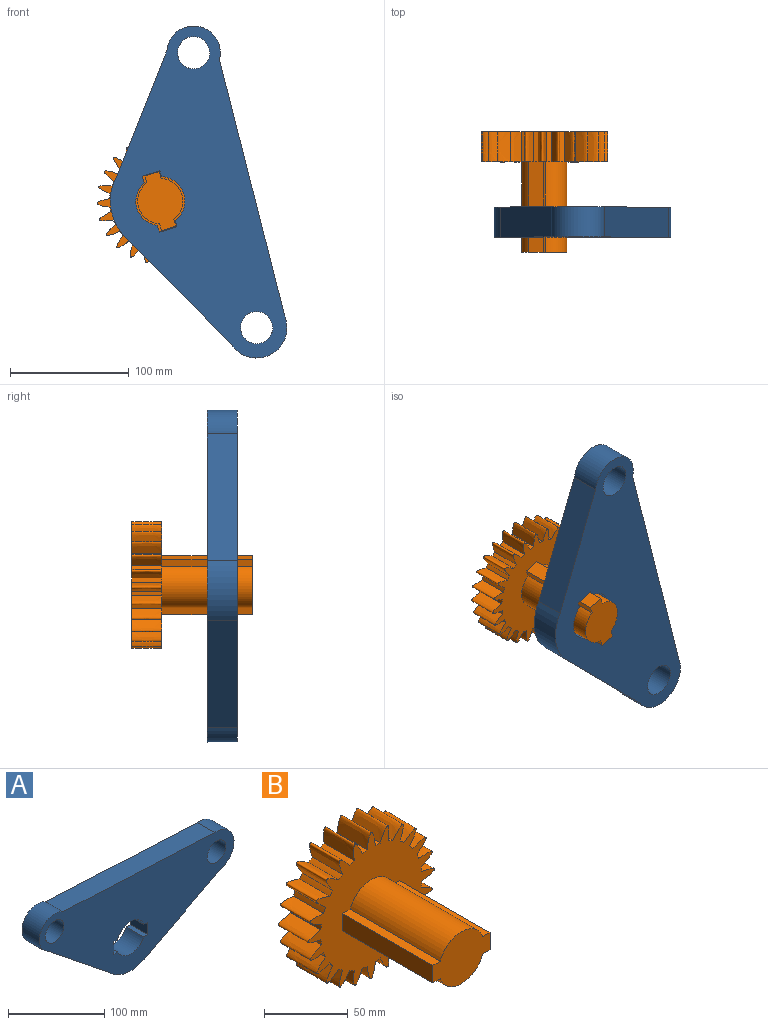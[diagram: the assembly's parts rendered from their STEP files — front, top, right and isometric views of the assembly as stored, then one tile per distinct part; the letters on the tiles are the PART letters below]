
ASSEMBLY  parts=2 mates=1
PART A: 18 faces, bbox 285.5x25.4x128.4 mm
  f0: plane 285.47x128.35mm, normal (0,-1,0), area 20341.7mm2, adj f2,f3,f4,f5,f6,f7,f8,f9
  f1: plane 285.47x128.35mm, normal (0,1,0), area 20341.7mm2, adj f2,f3,f4,f5,f6,f7,f8,f9
  f2: cylinder r=22.52mm len=43.27mm, axis (0,1,0), area 1890.6mm2, adj f0,f1,f3,f7
  f3: plane 89.47x71.82mm, normal (-0.63,0,-0.78), area 2914.1mm2, adj f0,f1,f2,f4
  f4: cylinder r=42.25mm len=50.29mm, axis (0,1,0), area 1390.7mm2, adj f0,f1,f3,f5
  f5: plane 112.86x58.95mm, normal (0.46,0,-0.89), area 3234.2mm2, adj f0,f1,f4,f6
  f6: cylinder r=25.63mm len=50.41mm, axis (0,1,0), area 1940.8mm2, adj f0,f1,f5,f7
  f7: plane 222.79x25.4mm, normal (0.05,0,1), area 5665.7mm2, adj f0,f1,f2,f6
  f8: cylinder r=20.68mm len=37.69mm, axis (0,1,0), area 1204.7mm2, adj f0,f1,f9,f15
  f9: plane 25.4x6.07mm, normal (0,0,1), area 154.1mm2, adj f0,f1,f8,f10
  f10: plane 25.4x15.55mm, normal (-1,0,0), area 395mm2, adj f0,f1,f9,f11
  f11: plane 25.4x5.48mm, normal (0,0,-1), area 139.1mm2, adj f0,f1,f10,f12
  f12: cylinder r=20.68mm len=38.87mm, axis (0,1,0), area 1284.4mm2, adj f0,f1,f11,f13
  f13: plane 25.4x5.13mm, normal (0,0,-1), area 130.4mm2, adj f0,f1,f12,f14
  f14: plane 25.4x15.55mm, normal (1,0,0), area 395mm2, adj f0,f1,f13,f15
  f15: plane 25.4x5.72mm, normal (0,0,1), area 145.3mm2, adj f0,f1,f8,f14
  f16: cylinder r=13.56mm len=27.13mm, axis (0,1,0), area 2164.7mm2, adj f0,f1
  f17: cylinder r=13.56mm len=27.13mm, axis (0,1,0), area 2164.7mm2, adj f0,f1
PART B: 59 faces, bbox 115x101.6x115 mm
  f0: plane 76.2x6.17mm, normal (0,0,1), area 470.1mm2, adj f1,f7,f8,f57
  f1: cylinder r=19.05mm len=76.2mm, axis (0,1,0), area 3573.7mm2, adj f0,f2,f8,f57
  f2: plane 76.2x6.17mm, normal (0,0,1), area 470.1mm2, adj f1,f3,f8,f57
  f3: plane 76.2x12.7mm, normal (-1,0,0), area 967.7mm2, adj f2,f4,f8,f57
  f4: plane 76.2x6.17mm, normal (0,0,-1), area 470.1mm2, adj f3,f5,f8,f57
  f5: cylinder r=19.05mm len=76.2mm, axis (0,1,0), area 3573.7mm2, adj f4,f6,f8,f57
  f6: plane 76.2x6.17mm, normal (0,0,-1), area 470.1mm2, adj f5,f7,f8,f57
  f7: plane 76.2x12.7mm, normal (1,0,0), area 967.7mm2, adj f0,f6,f8,f57
  f8: plane 48.26x38.1mm, normal (0,-1,0), area 1278.2mm2, adj f0,f1,f2,f3,f4,f5,f6,f7
  f9: extruded ~25.4x11.41mm, area 595.6mm2, adj f10,f56,f57,f58
  f10: cylinder r=42.74mm len=25.4mm, axis (0,1,0), area 102mm2, adj f9,f11,f57,f58
  f11: extruded ~25.4x11.26mm, area 595.6mm2, adj f10,f12,f57,f58
  f12: cylinder r=42.74mm len=25.4mm, axis (0,1,0), area 102mm2, adj f11,f13,f57,f58
  f13: extruded ~25.4x10.41mm, area 595.6mm2, adj f12,f14,f57,f58
  f14: cylinder r=42.74mm len=25.4mm, axis (0,1,0), area 102mm2, adj f13,f15,f57,f58
  f15: extruded ~25.4x11.25mm, area 595.6mm2, adj f14,f16,f57,f58
  f16: cylinder r=42.74mm len=25.4mm, axis (0,1,0), area 102mm2, adj f15,f17,f57,f58
  f17: extruded ~25.4x11.41mm, area 595.6mm2, adj f16,f18,f57,f58
  f18: cylinder r=42.74mm len=25.4mm, axis (0,1,0), area 102mm2, adj f17,f19,f57,f58
  f19: extruded ~25.4x10.84mm, area 595.6mm2, adj f18,f20,f57,f58
  f20: cylinder r=42.74mm len=25.4mm, axis (0,1,0), area 102mm2, adj f19,f21,f57,f58
  f21: extruded ~25.4x11.41mm, area 595.6mm2, adj f20,f22,f57,f58
  f22: cylinder r=42.74mm len=25.4mm, axis (0,1,0), area 102mm2, adj f21,f23,f57,f58
  f23: extruded ~25.4x11.26mm, area 595.6mm2, adj f22,f24,f57,f58
  f24: cylinder r=42.74mm len=25.4mm, axis (0,1,0), area 102mm2, adj f23,f25,f57,f58
  f25: extruded ~25.4x10.41mm, area 595.6mm2, adj f24,f26,f57,f58
  f26: cylinder r=42.74mm len=25.4mm, axis (0,1,0), area 102mm2, adj f25,f27,f57,f58
  f27: extruded ~25.4x11.25mm, area 595.6mm2, adj f26,f28,f57,f58
  f28: cylinder r=42.74mm len=25.4mm, axis (0,1,0), area 102mm2, adj f27,f29,f57,f58
  f29: extruded ~25.4x11.41mm, area 595.6mm2, adj f28,f30,f57,f58
  f30: cylinder r=42.74mm len=25.4mm, axis (0,1,0), area 102mm2, adj f29,f31,f57,f58
  f31: extruded ~25.4x10.84mm, area 595.6mm2, adj f30,f32,f57,f58
  f32: cylinder r=42.74mm len=25.4mm, axis (0,1,0), area 102mm2, adj f31,f33,f57,f58
  f33: extruded ~25.4x11.41mm, area 595.6mm2, adj f32,f34,f57,f58
  f34: cylinder r=42.74mm len=25.4mm, axis (0,1,0), area 102mm2, adj f33,f35,f57,f58
  f35: extruded ~25.4x11.26mm, area 595.6mm2, adj f34,f36,f57,f58
  f36: cylinder r=42.74mm len=25.4mm, axis (0,1,0), area 102mm2, adj f35,f37,f57,f58
  f37: extruded ~25.4x10.41mm, area 595.6mm2, adj f36,f38,f57,f58
  f38: cylinder r=42.74mm len=25.4mm, axis (0,1,0), area 102mm2, adj f37,f39,f57,f58
  f39: extruded ~25.4x11.25mm, area 595.6mm2, adj f38,f40,f57,f58
  f40: cylinder r=42.74mm len=25.4mm, axis (0,1,0), area 102mm2, adj f39,f41,f57,f58
  f41: extruded ~25.4x11.41mm, area 595.6mm2, adj f40,f42,f57,f58
  f42: cylinder r=42.74mm len=25.4mm, axis (0,1,0), area 102mm2, adj f41,f43,f57,f58
  f43: extruded ~25.4x10.84mm, area 595.6mm2, adj f42,f44,f57,f58
  f44: cylinder r=42.74mm len=25.4mm, axis (0,1,0), area 102mm2, adj f43,f45,f57,f58
  f45: extruded ~25.4x11.41mm, area 595.6mm2, adj f44,f46,f57,f58
  f46: cylinder r=42.74mm len=25.4mm, axis (0,1,0), area 102mm2, adj f45,f47,f57,f58
  f47: extruded ~25.4x11.26mm, area 595.6mm2, adj f46,f48,f57,f58
  f48: cylinder r=42.74mm len=25.4mm, axis (0,1,0), area 102mm2, adj f47,f49,f57,f58
  f49: extruded ~25.4x10.41mm, area 595.6mm2, adj f48,f50,f57,f58
  f50: cylinder r=42.74mm len=25.4mm, axis (0,1,0), area 102mm2, adj f49,f51,f57,f58
  f51: extruded ~25.4x11.25mm, area 595.6mm2, adj f50,f52,f57,f58
  f52: cylinder r=42.74mm len=25.4mm, axis (0,1,0), area 102mm2, adj f51,f53,f57,f58
  f53: extruded ~25.4x11.41mm, area 595.6mm2, adj f52,f54,f57,f58
  f54: cylinder r=42.74mm len=25.4mm, axis (0,1,0), area 102mm2, adj f53,f55,f57,f58
  f55: extruded ~25.4x10.84mm, area 595.6mm2, adj f54,f56,f57,f58
  f56: cylinder r=42.74mm len=25.4mm, axis (0,1,0), area 102mm2, adj f9,f55,f57,f58
  f57: plane 114.97x114.97mm, normal (0,-1,0), area 5684.9mm2, adj f0,f1,f2,f3,f4,f5,f6,f7
  f58: plane 114.97x114.97mm, normal (0,1,0), area 6963.1mm2, adj f9,f10,f11,f12,f13,f14,f15,f16
PLACE A rot(axis=(0,1,0),72.9deg) t=(-9.71,-22.3,-24.19)mm
PLACE B rot(axis=(0,1,0),72.9deg) t=(-9.71,41.2,-24.19)mm
MATE fastened A.f4 <-> B.f1  axis (0,1,0) through (-9.71,-22.3,-24.19)mm
